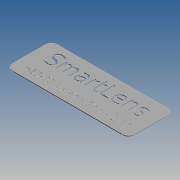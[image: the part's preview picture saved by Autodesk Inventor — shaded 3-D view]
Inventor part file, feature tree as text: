
AUTODESK INVENTOR PART (.ipt)
format: ipt  version: 2019 (Build 230136000, 136)  size: 831,488 bytes
history: native  units: mm
features: extrude x2, sketch x2, fillet x1
ambient origin geometry x8: Origin, YZ Plane, XZ Plane, XY Plane, X Axis, Y Axis, Z Axis, Center Point
bodies: Solid1 (feature_tree)
feature tree (5):
  extrude  "Extrusion1"  Depth=0.4mm
  fillet  "Fillet1"  Radius=0.4mm
  extrude  "Extrusion2"  Depth=0.4mm TaperAngle=0.0deg
  sketch  "Sketch1"  dims[d0=39.5mm d1=14.5mm d2=0.4mm d3=0.0mm]
  sketch  "Sketch2"  dims[d4=2.0mm d5=0.4mm d6=0.0mm]
